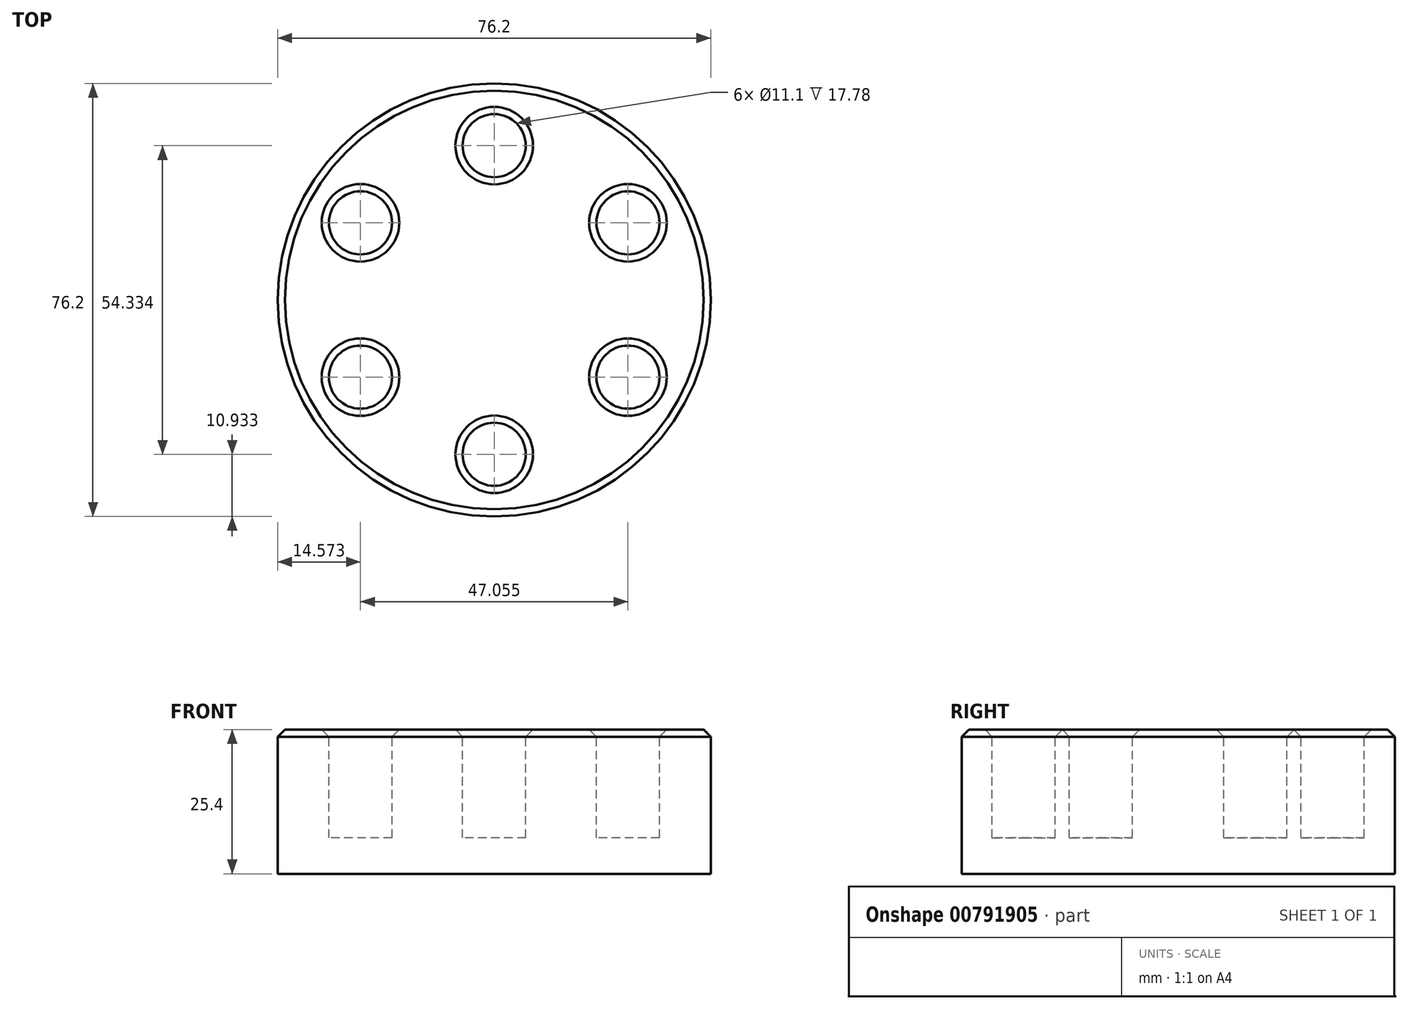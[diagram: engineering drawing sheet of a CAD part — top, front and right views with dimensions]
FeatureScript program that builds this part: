
annotation { "Feature Type Name" : "Feature", "Feature Type Description" : "" }
export const myFeature = defineFeature(function(context is Context, id is Id, definition is map)
    precondition{}
    {
        {
            var Q0;
            Q0=qCreatedBy(makeId("Top.planeOp"),FACE);
            var sketch = newSketch(context, id + "F0", { "sketchPlane" : qUnion([Q0])});
            skCircle(sketch, "E0", {"center": v(0, 0) * mm, "radius": 38.1 * mm});
            skSolve(sketch);
        }
        {
            var Q0;
            Q0 = qSketchRegion(id + "F0", true);
            extrude(context, id + "F1", {"entities" : qUnion([Q0]), "depth" : 25.4 * mm, "offsetDistance" : 25.4 * mm});
        }
        {
            var Q0;
            Q0=makeQuery(id+"F1.opExtrude","CAP_FACE",FACE,{"disambiguationData":[OSD([sQuery(id+"F0.wireOp",EDGE,"E0")])],"isStart":false});
            var sketch = newSketch(context, id + "F2", { "sketchPlane" : qUnion([Q0])});
            skCircle(sketch, "E1", {"center": v(0, 27.17) * mm, "radius": 5.55 * mm});
            skCircle(sketch, "E2.1.0", {"center": v(-23.53, 13.58) * mm, "radius": 5.55 * mm});
            skCircle(sketch, "E2.2.0", {"center": v(-23.53, -13.58) * mm, "radius": 5.55 * mm});
            skCircle(sketch, "E2.3.0", {"center": v(0, -27.17) * mm, "radius": 5.55 * mm});
            skCircle(sketch, "E2.4.0", {"center": v(23.53, -13.58) * mm, "radius": 5.55 * mm});
            skCircle(sketch, "E2.5.0", {"center": v(23.53, 13.58) * mm, "radius": 5.55 * mm});
            skPoint(sketch, "E2.center", {"position": v(0, 0) * mm});
            skSolve(sketch);
        }
        {
            var Q0;
            Q0 = qSketchRegion(id + "F2", true);
            extrude(context, id + "F3", {"entities" : qUnion([Q0]), "operationType" : NewBodyOperationType.REMOVE, "oppositeDirection" : true, "depth" : 19.05 * mm, "offsetDistance" : 25.4 * mm});
        }
        {
            var Q0;
            Q0=makeQuery(id+"F3.boolean.opBoolean","COPY",EDGE,{"derivedFrom":makeQuery(id+"F3.opExtrude","CAP_EDGE",EDGE,{"disambiguationData":[OSD([sQuery(id+"F2.wireOp",EDGE,"E1")])],"isStart":true})});
            var Q1;
            Q1=makeQuery(id+"F1.opExtrude","CAP_FACE",FACE,{"disambiguationData":[OSD([sQuery(id+"F0.wireOp",EDGE,"E0")])],"isStart":false});
            chamfer(context, id + "F4", {"entities" : qUnion([Q0, Q1]), "width" : 1.27 * mm, "tangentPropagation" : true});
        }
    });
